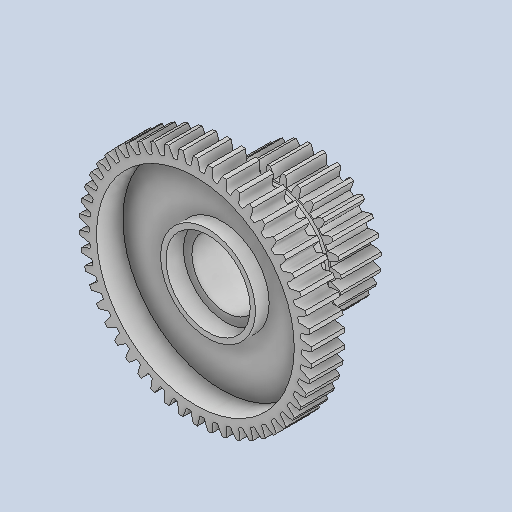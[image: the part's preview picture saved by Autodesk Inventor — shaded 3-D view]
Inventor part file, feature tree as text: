
AUTODESK INVENTOR PART (.ipt)
format: ipt  version: 2022.3 (Build 263350000, 350)  size: 629,248 bytes
history: native  units: in
note: dims shown in document units (in); Inventor stores cm internally (conversion verified against a paired STEP export)
features: chamfer x1
ambient origin geometry x8: Origin, YZ Plane, XZ Plane, XY Plane, X Axis, Y Axis, Z Axis, Center Point
bodies: Solid1 (feature_tree)
feature tree (1):
  chamfer  "Chamfer2"  [1 undecoded]
note: 1 required parameter value undecoded (feature->parameter linkage not recoverable at this tier; creation-order binding heuristic only, values carry confidence <= 0.55)
